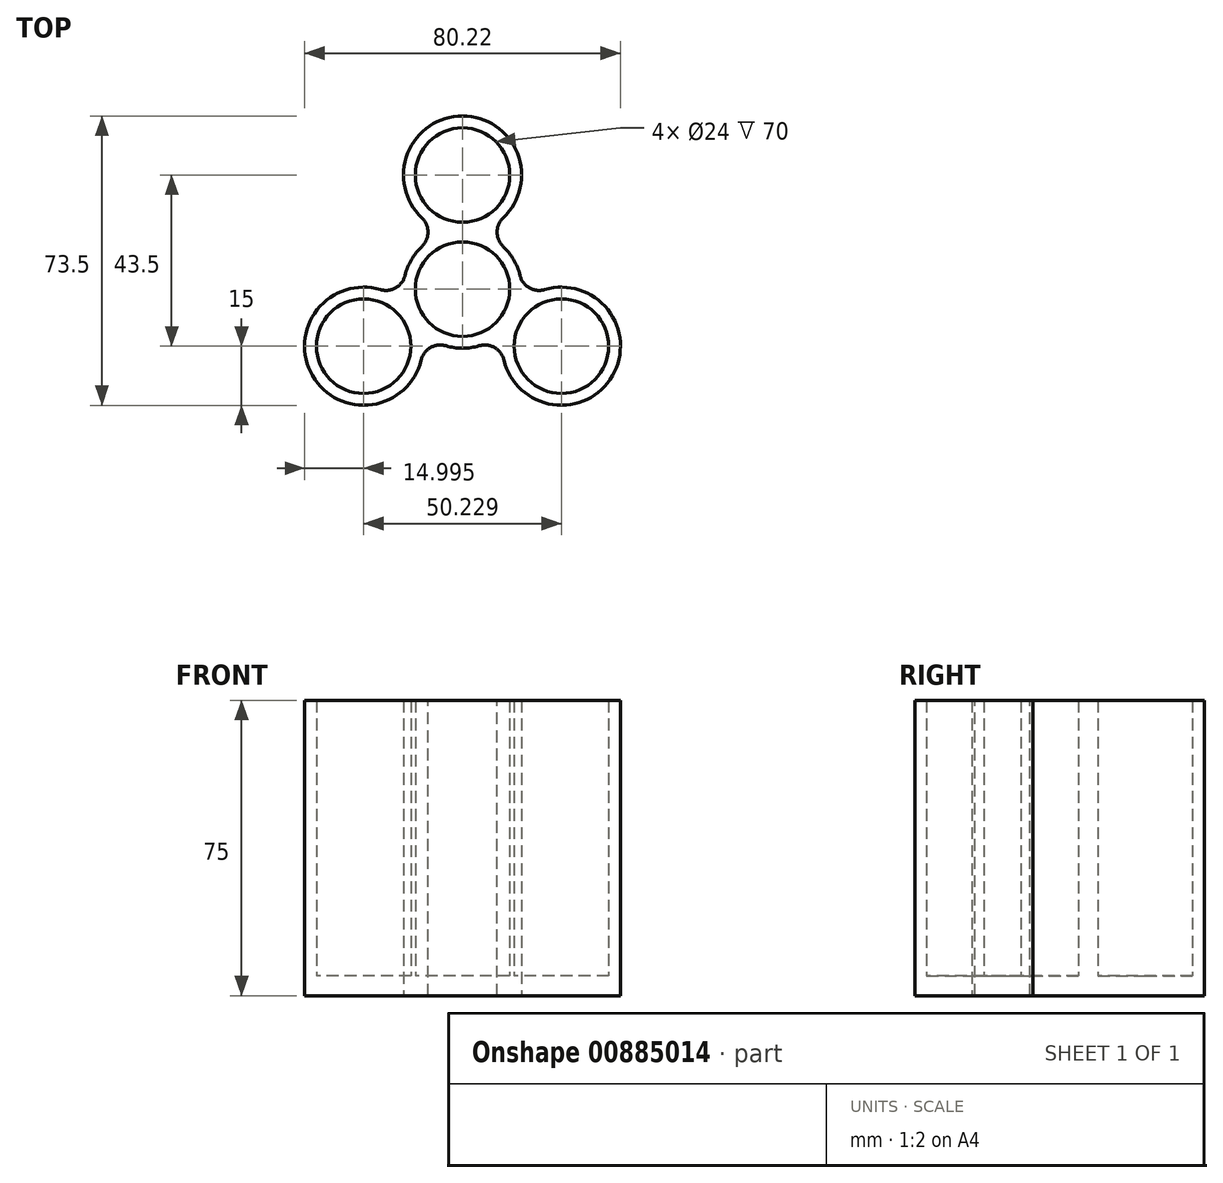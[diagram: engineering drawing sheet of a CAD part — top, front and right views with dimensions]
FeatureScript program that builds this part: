
annotation { "Feature Type Name" : "Feature", "Feature Type Description" : "" }
export const myFeature = defineFeature(function(context is Context, id is Id, definition is map)
    precondition{}
    {
        {
            var Q0;
            Q0=qCreatedBy(makeId("Top.planeOp"),FACE);
            var sketch = newSketch(context, id + "F0", { "sketchPlane" : qUnion([Q0])});
            skArc(sketch, "E0", {"start": v(14.48, -3.92) * mm, "mid": v(13, 7.5) * mm, "end": v(3.84, 14.5) * mm});
            skCircle(sketch, "E1", {"center": v(0, 0) * mm, "radius": 12 * mm});
            skArc(sketch, "E2", {"start": v(3.84, 14.5) * mm, "mid": v(0, 44) * mm, "end": v(-3.84, 14.5) * mm});
            skPoint(sketch, "E2.first.point", {"position": v(0, 14) * mm});
            skPoint(sketch, "E2.second.point", {"position": v(0, 44) * mm});
            skArc(sketch, "E3", {"start": v(10.64, -10.58) * mm, "mid": v(38.1, -22) * mm, "end": v(14.48, -3.92) * mm});
            skArc(sketch, "E4", {"start": v(-14.48, -3.92) * mm, "mid": v(-38.1, -22) * mm, "end": v(-10.64, -10.58) * mm});
            skLineSegment(sketch, "E5", {"start": v(0, 0) * mm, "end": v(47.62, -27.5) * mm, "construction": true});
            skLineSegment(sketch, "E6", {"start": v(0, 0) * mm, "end": v(-50.23, -29) * mm, "construction": true});
            skCircle(sketch, "E7", {"center": v(-25.11, -14.5) * mm, "radius": 12 * mm});
            skCircle(sketch, "E8", {"center": v(25.11, -14.5) * mm, "radius": 12 * mm});
            skCircle(sketch, "E9", {"center": v(0, 29) * mm, "radius": 12 * mm});
            skArc(sketch, "E10.trimOffspring", {"start": v(-3.84, 14.5) * mm, "mid": v(-13, 7.5) * mm, "end": v(-14.48, -3.92) * mm});
            skArc(sketch, "E11.trimOffspring", {"start": v(-10.64, -10.58) * mm, "mid": v(0, -15) * mm, "end": v(10.64, -10.58) * mm});
            skSolve(sketch);
        }
        {
            var Q0;
            Q0=makeQuery(id+"F0.imprint","IMPRINT",FACE,{"disambiguationData":[TD([[makeQuery(id+"F0.imprint","IMPRINT",EDGE,{"derivedFrom":sQuery(id+"F0.wireOp",EDGE,"E0")}),1.0]])]});
            var Q1;
            Q1=makeQuery(id+"F0.imprint","IMPRINT",FACE,{"disambiguationData":[TD([[makeQuery(id+"F0.imprint","IMPRINT",EDGE,{"derivedFrom":sQuery(id+"F0.wireOp",EDGE,"E8")}),1.0]])]});
            var Q2;
            Q2=makeQuery(id+"F0.imprint","IMPRINT",FACE,{"disambiguationData":[TD([[makeQuery(id+"F0.imprint","IMPRINT",EDGE,{"derivedFrom":sQuery(id+"F0.wireOp",EDGE,"E1")}),1.0]])]});
            var Q3;
            Q3=makeQuery(id+"F0.imprint","IMPRINT",FACE,{"disambiguationData":[TD([[makeQuery(id+"F0.imprint","IMPRINT",EDGE,{"derivedFrom":sQuery(id+"F0.wireOp",EDGE,"E9")}),1.0]])]});
            var Q4;
            Q4=makeQuery(id+"F0.imprint","IMPRINT",FACE,{"disambiguationData":[TD([[makeQuery(id+"F0.imprint","IMPRINT",EDGE,{"derivedFrom":sQuery(id+"F0.wireOp",EDGE,"E7")}),1.0]])]});
            extrude(context, id + "F1", {"entities" : qUnion([Q0, Q1, Q2, Q3, Q4]), "depth" : 5 * mm, "offsetDistance" : 25 * mm});
        }
        {
            var Q0;
            Q0=makeQuery(id+"F0.imprint","IMPRINT",FACE,{"disambiguationData":[TD([[makeQuery(id+"F0.imprint","IMPRINT",EDGE,{"derivedFrom":sQuery(id+"F0.wireOp",EDGE,"E0")}),1.0]])]});
            extrude(context, id + "F2", {"entities" : qUnion([Q0]), "operationType" : NewBodyOperationType.ADD, "depth" : 75 * mm, "offsetDistance" : 25 * mm});
        }
        {
            var Q0;
            {var subQ0=sQuery(id+"F0.wireOp",EDGE,"E2");var subQ1=sQuery(id+"F0.wireOp",EDGE,"E0");Q0=makeQuery(id+"F2.boolean.opBoolean","MERGE",EDGE,{"derivedFrom":[makeQuery(id+"F1.opExtrude","SWEPT_EDGE",EDGE,{"disambiguationData":[OSD([subQ1,subQ0])]}),makeQuery(id+"F2.opExtrude","SWEPT_EDGE",EDGE,{"disambiguationData":[OSD([subQ1,subQ0])]})]});}
            var Q1;
            {var subQ0=sQuery(id+"F0.wireOp",EDGE,"E3");var subQ1=sQuery(id+"F0.wireOp",EDGE,"E0");Q1=makeQuery(id+"F2.boolean.opBoolean","MERGE",EDGE,{"derivedFrom":[makeQuery(id+"F1.opExtrude","SWEPT_EDGE",EDGE,{"disambiguationData":[OSD([subQ1,subQ0])]}),makeQuery(id+"F2.opExtrude","SWEPT_EDGE",EDGE,{"disambiguationData":[OSD([subQ1,subQ0])]})]});}
            var Q2;
            {var subQ0=sQuery(id+"F0.wireOp",EDGE,"E11.trimOffspring");var subQ1=sQuery(id+"F0.wireOp",EDGE,"E3");Q2=makeQuery(id+"F2.boolean.opBoolean","MERGE",EDGE,{"derivedFrom":[makeQuery(id+"F1.opExtrude","SWEPT_EDGE",EDGE,{"disambiguationData":[OSD([subQ1,subQ0])]}),makeQuery(id+"F2.opExtrude","SWEPT_EDGE",EDGE,{"disambiguationData":[OSD([subQ1,subQ0])]})]});}
            var Q3;
            {var subQ0=sQuery(id+"F0.wireOp",EDGE,"E11.trimOffspring");var subQ1=sQuery(id+"F0.wireOp",EDGE,"E4");Q3=makeQuery(id+"F2.boolean.opBoolean","MERGE",EDGE,{"derivedFrom":[makeQuery(id+"F1.opExtrude","SWEPT_EDGE",EDGE,{"disambiguationData":[OSD([subQ1,subQ0])]}),makeQuery(id+"F2.opExtrude","SWEPT_EDGE",EDGE,{"disambiguationData":[OSD([subQ1,subQ0])]})]});}
            var Q4;
            {var subQ0=sQuery(id+"F0.wireOp",EDGE,"E10.trimOffspring");var subQ1=sQuery(id+"F0.wireOp",EDGE,"E4");Q4=makeQuery(id+"F2.boolean.opBoolean","MERGE",EDGE,{"derivedFrom":[makeQuery(id+"F1.opExtrude","SWEPT_EDGE",EDGE,{"disambiguationData":[OSD([subQ1,subQ0])]}),makeQuery(id+"F2.opExtrude","SWEPT_EDGE",EDGE,{"disambiguationData":[OSD([subQ1,subQ0])]})]});}
            var Q5;
            {var subQ0=sQuery(id+"F0.wireOp",EDGE,"E10.trimOffspring");var subQ1=sQuery(id+"F0.wireOp",EDGE,"E2");Q5=makeQuery(id+"F2.boolean.opBoolean","MERGE",EDGE,{"derivedFrom":[makeQuery(id+"F1.opExtrude","SWEPT_EDGE",EDGE,{"disambiguationData":[OSD([subQ1,subQ0])]}),makeQuery(id+"F2.opExtrude","SWEPT_EDGE",EDGE,{"disambiguationData":[OSD([subQ1,subQ0])]})]});}
            fillet(context, id + "F3", {"entities" : qUnion([Q0, Q1, Q2, Q3, Q4, Q5]), "radius" : 5 * mm, "tangentPropagation" : true, "allowEdgeOverflow" : false});
        }
    });
